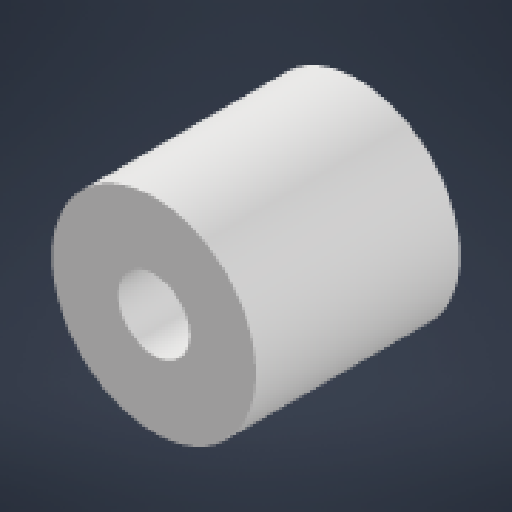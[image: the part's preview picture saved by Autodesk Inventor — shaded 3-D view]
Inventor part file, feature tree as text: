
AUTODESK INVENTOR PART (.ipt)
format: ipt  version: 2024.1 (Build 281209000, 209)  size: 123,392 bytes
history: native  units: in
note: dims shown in document units (in); Inventor stores cm internally (conversion verified against a paired STEP export)
features: extrude x1, sketch x1
ambient origin geometry x8: Origin, YZ Plane, XZ Plane, XY Plane, X Axis, Y Axis, Z Axis, Center Point
bodies: Solid1 (feature_tree)
feature tree (2):
  extrude  "Extrusion1"  Depth=0.73in
  sketch  "Sketch1"  dims[d0=0.254in d1=0.73in d2=0.73in d3=0.0in]
